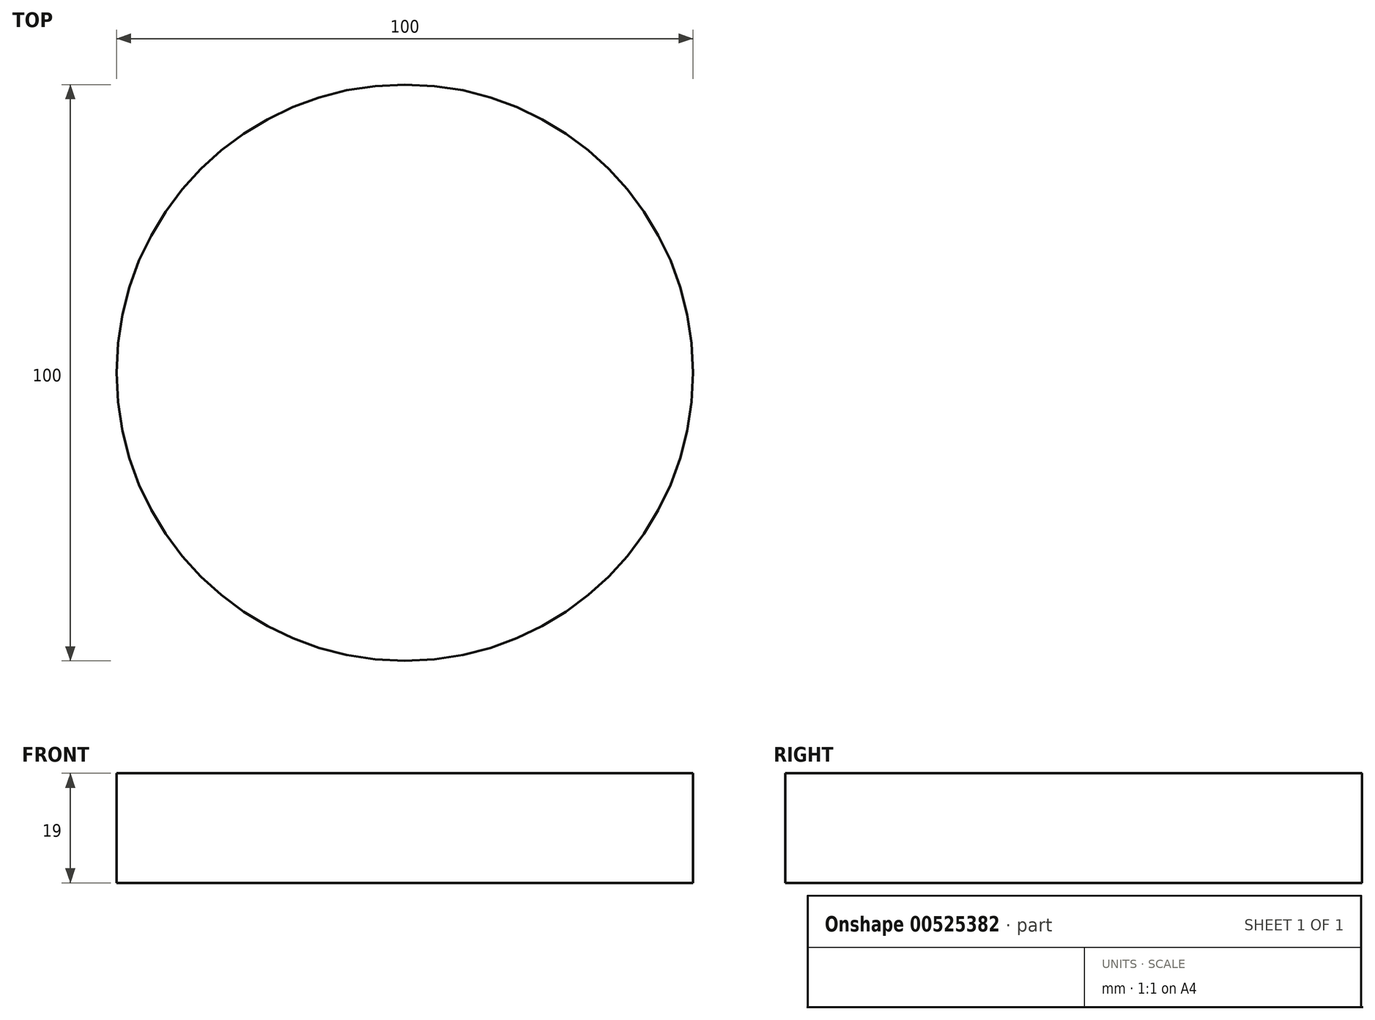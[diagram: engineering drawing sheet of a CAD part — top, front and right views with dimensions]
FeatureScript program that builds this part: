
annotation { "Feature Type Name" : "Feature", "Feature Type Description" : "" }
export const myFeature = defineFeature(function(context is Context, id is Id, definition is map)
    precondition{}
    {
        {
            var Q0;
            Q0=qCreatedBy(makeId("Top.planeOp"),FACE);
            var sketch = newSketch(context, id + "F0", { "sketchPlane" : qUnion([Q0])});
            skCircle(sketch, "E0", {"center": v(0, 0) * mm, "radius": 50 * mm});
            skSolve(sketch);
        }
        {
            var Q0;
            Q0=makeQuery(id+"F0.imprint","IMPRINT",FACE,{"disambiguationData":[TD([[makeQuery(id+"F0.imprint","IMPRINT",EDGE,{"derivedFrom":sQuery(id+"F0.wireOp",EDGE,"E0")}),1.0]])]});
            extrude(context, id + "F1", {"entities" : qUnion([Q0]), "depth" : 19 * mm, "offsetDistance" : 25 * mm});
        }
    });
